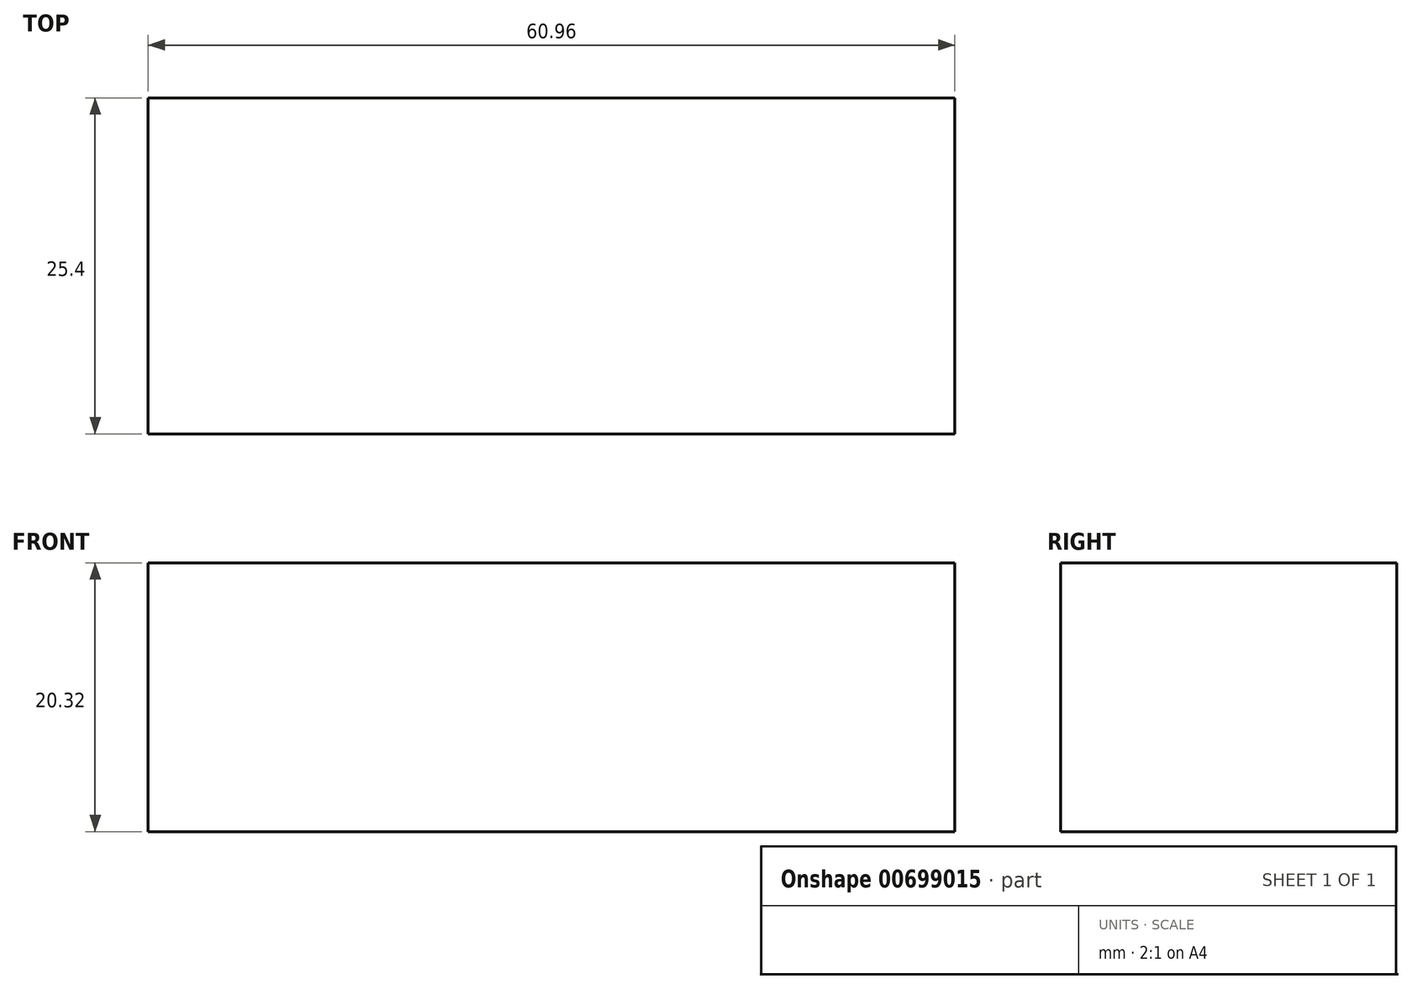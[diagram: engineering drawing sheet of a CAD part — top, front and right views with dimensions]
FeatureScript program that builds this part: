
annotation { "Feature Type Name" : "Feature", "Feature Type Description" : "" }
export const myFeature = defineFeature(function(context is Context, id is Id, definition is map)
    precondition{}
    {
        {
            var Q0;
            Q0=qCreatedBy(makeId("Front.planeOp"),FACE);
            var sketch = newSketch(context, id + "F0", { "sketchPlane" : qUnion([Q0])});
            skLineSegment(sketch, "E0.bottom", {"start": v(-60.96, 58.11) * mm, "end": v(-40.64, 58.11) * mm});
            skLineSegment(sketch, "E0.top", {"start": v(-60.96, 37.8) * mm, "end": v(-40.64, 37.8) * mm});
            skLineSegment(sketch, "E0.left", {"start": v(-60.96, 58.11) * mm, "end": v(-60.96, 37.8) * mm});
            skLineSegment(sketch, "E0.right", {"start": v(-40.64, 58.11) * mm, "end": v(-40.64, 37.8) * mm});
            skLineSegment(sketch, "E1.bottom", {"start": v(-40.64, 58.11) * mm, "end": v(-20.32, 58.11) * mm});
            skLineSegment(sketch, "E1.top", {"start": v(-40.64, 37.8) * mm, "end": v(-20.32, 37.8) * mm});
            skLineSegment(sketch, "E1.right", {"start": v(-20.32, 58.11) * mm, "end": v(-20.32, 37.8) * mm});
            skLineSegment(sketch, "E2.top", {"start": v(-60.96, 17.47) * mm, "end": v(-40.64, 17.47) * mm});
            skLineSegment(sketch, "E2.left", {"start": v(-60.96, 37.8) * mm, "end": v(-60.96, 17.47) * mm});
            skLineSegment(sketch, "E2.right", {"start": v(-40.64, 37.8) * mm, "end": v(-40.64, 17.47) * mm});
            skLineSegment(sketch, "E3.top", {"start": v(-40.64, 17.47) * mm, "end": v(-20.32, 17.47) * mm});
            skLineSegment(sketch, "E3.right", {"start": v(-20.32, 37.8) * mm, "end": v(-20.32, 17.47) * mm});
            skLineSegment(sketch, "E4.bottom", {"start": v(-20.32, 58.11) * mm, "end": v(0, 58.11) * mm});
            skLineSegment(sketch, "E4.top", {"start": v(-20.32, 37.8) * mm, "end": v(0, 37.8) * mm});
            skLineSegment(sketch, "E4.right", {"start": v(0, 58.11) * mm, "end": v(0, 37.8) * mm});
            skLineSegment(sketch, "E5.top", {"start": v(-20.32, 17.66) * mm, "end": v(0, 17.66) * mm});
            skLineSegment(sketch, "E5.left", {"start": v(-20.32, 37.8) * mm, "end": v(-20.32, 17.66) * mm});
            skLineSegment(sketch, "E5.right", {"start": v(0, 37.8) * mm, "end": v(0, 17.66) * mm});
            skSolve(sketch);
        }
        {
            var Q0;
            Q0 = qSketchRegion(id + "F0", true);
            extrude(context, id + "F1", {"entities" : qUnion([Q0]), "depth" : 25.4 * mm, "offsetDistance" : 25.4 * mm});
        }
        {
            var Q0;
            Q0=makeQuery(id+"F1.opExtrude","SWEPT_BODY",BODY,{"disambiguationData":[OSD([sQuery(id+"F0.wireOp",EDGE,"E0.bottom"),sQuery(id+"F0.wireOp",EDGE,"E0.left"),sQuery(id+"F0.wireOp",EDGE,"E1.bottom"),sQuery(id+"F0.wireOp",EDGE,"E2.top"),sQuery(id+"F0.wireOp",EDGE,"E2.left"),sQuery(id+"F0.wireOp",EDGE,"E3.top"),sQuery(id+"F0.wireOp",EDGE,"E3.right"),sQuery(id+"F0.wireOp",EDGE,"E4.bottom"),sQuery(id+"F0.wireOp",EDGE,"E4.right"),sQuery(id+"F0.wireOp",EDGE,"E5.top"),sQuery(id+"F0.wireOp",EDGE,"E5.right")])]});
            deleteBodies(context, id + "F2", {"entities" : qUnion([Q0])});
        }
        {
            var Q0;
            Q0=qCreatedBy(makeId("Front.planeOp"),FACE);
            var sketch = newSketch(context, id + "F3", { "sketchPlane" : qUnion([Q0])});
            skLineSegment(sketch, "E6.bottom", {"start": v(-68.35, 59.37) * mm, "end": v(-48.03, 59.37) * mm});
            skLineSegment(sketch, "E6.top", {"start": v(-68.35, 39.05) * mm, "end": v(-48.03, 39.05) * mm});
            skLineSegment(sketch, "E6.left", {"start": v(-68.35, 59.37) * mm, "end": v(-68.35, 39.05) * mm});
            skLineSegment(sketch, "E6.right", {"start": v(-48.03, 59.37) * mm, "end": v(-48.03, 39.05) * mm});
            skLineSegment(sketch, "E7.bottom", {"start": v(-48.03, 59.37) * mm, "end": v(-27.7, 59.37) * mm});
            skLineSegment(sketch, "E7.top", {"start": v(-48.03, 39.05) * mm, "end": v(-27.7, 39.05) * mm});
            skLineSegment(sketch, "E7.right", {"start": v(-27.7, 59.37) * mm, "end": v(-27.7, 39.05) * mm});
            skLineSegment(sketch, "E8.bottom", {"start": v(-27.7, 59.37) * mm, "end": v(-7.39, 59.37) * mm});
            skLineSegment(sketch, "E8.top", {"start": v(-27.7, 39.05) * mm, "end": v(-7.39, 39.05) * mm});
            skLineSegment(sketch, "E8.right", {"start": v(-7.39, 59.37) * mm, "end": v(-7.39, 39.05) * mm});
            skSolve(sketch);
        }
        {
            var Q0;
            Q0 = qSketchRegion(id + "F3", true);
            extrude(context, id + "F4", {"entities" : qUnion([Q0]), "depth" : 25.4 * mm, "offsetDistance" : 25.4 * mm});
        }
        {
            var Q0;
            Q0=qCreatedBy(makeId("Front.planeOp"),FACE);
            var sketch = newSketch(context, id + "F5", { "sketchPlane" : qUnion([Q0])});
            skCircle(sketch, "E9", {"center": v(-58.53, 48.98) * mm, "radius": 7.62 * mm});
            skCircle(sketch, "E10", {"center": v(-38.48, 48.98) * mm, "radius": 7.62 * mm});
            skCircle(sketch, "E11", {"center": v(-17.47, 48.98) * mm, "radius": 7.62 * mm});
            skSolve(sketch);
        }
        {
            var Q0;
            Q0 = qSketchRegion(id + "F5", true);
            extrude(context, id + "F6", {"entities" : qUnion([Q0]), "operationType" : NewBodyOperationType.REMOVE, "oppositeDirection" : true, "depth" : 25.4 * mm, "offsetDistance" : 25.4 * mm});
        }
        {
            var Q0;
            Q0=qCreatedBy(makeId("Front.planeOp"),FACE);
            var sketch = newSketch(context, id + "F7", { "sketchPlane" : qUnion([Q0])});
            skCircle(sketch, "E12", {"center": v(-58.53, 49.36) * mm, "radius": 6.35 * mm});
            skCircle(sketch, "E13", {"center": v(-40.58, 49.36) * mm, "radius": 6.35 * mm});
            skCircle(sketch, "E14", {"center": v(-22.44, 49.36) * mm, "radius": 6.35 * mm});
            skSolve(sketch);
        }
        {
            var Q0;
            Q0 = qSketchRegion(id + "F7", true);
            extrude(context, id + "F8", {"entities" : qUnion([Q0]), "operationType" : NewBodyOperationType.REMOVE, "oppositeDirection" : true, "depth" : 25.4 * mm, "offsetDistance" : 25.4 * mm});
        }
        {
            var Q0;
            Q0=qCreatedBy(makeId("Front.planeOp"),FACE);
            var sketch = newSketch(context, id + "F9", { "sketchPlane" : qUnion([Q0])});
            skCircle(sketch, "E15", {"center": v(-59.1, 49.93) * mm, "radius": 6.35 * mm});
            skCircle(sketch, "E16", {"center": v(-41.15, 49.93) * mm, "radius": 6.35 * mm});
            skCircle(sketch, "E17", {"center": v(-23.77, 49.93) * mm, "radius": 6.35 * mm});
            skSolve(sketch);
        }
        {
            var Q0;
            Q0 = qSketchRegion(id + "F9", true);
            extrude(context, id + "F10", {"entities" : qUnion([Q0]), "operationType" : NewBodyOperationType.REMOVE, "oppositeDirection" : true, "depth" : 25.4 * mm, "offsetDistance" : 25.4 * mm});
        }
        {
            var Q0;
            Q0=qCreatedBy(makeId("Front.planeOp"),FACE);
            var sketch = newSketch(context, id + "F11", { "sketchPlane" : qUnion([Q0])});
            skCircle(sketch, "E18", {"center": v(-59.48, 49.17) * mm, "radius": 6.35 * mm});
            skCircle(sketch, "E19", {"center": v(-41.91, 49.17) * mm, "radius": 6.35 * mm});
            skCircle(sketch, "E20", {"center": v(-22.06, 49.17) * mm, "radius": 6.35 * mm});
            skSolve(sketch);
        }
        {
            var Q0;
            Q0 = qSketchRegion(id + "F11", true);
            extrude(context, id + "F12", {"entities" : qUnion([Q0]), "operationType" : NewBodyOperationType.REMOVE, "oppositeDirection" : true, "depth" : 25.4 * mm, "offsetDistance" : 25.4 * mm});
        }
    });
